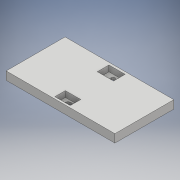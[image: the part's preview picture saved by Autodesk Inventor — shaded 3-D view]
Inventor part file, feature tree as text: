
AUTODESK INVENTOR PART (.ipt)
format: ipt  version: 2017 (Build 210142000, 142)  size: 264,704 bytes
history: native  units: mm
features: extrude x2, sketch x1
ambient origin geometry x8: Origin, YZ Plane, XZ Plane, XY Plane, X Axis, Y Axis, Z Axis, Center Point
bodies: Solido1 (feature_tree)
feature tree (3):
  extrude  "Estrusione1"  Depth=120.0mm
  extrude  "Estrusione2"  Depth=65.0mm
  sketch  "Schizzo2"
